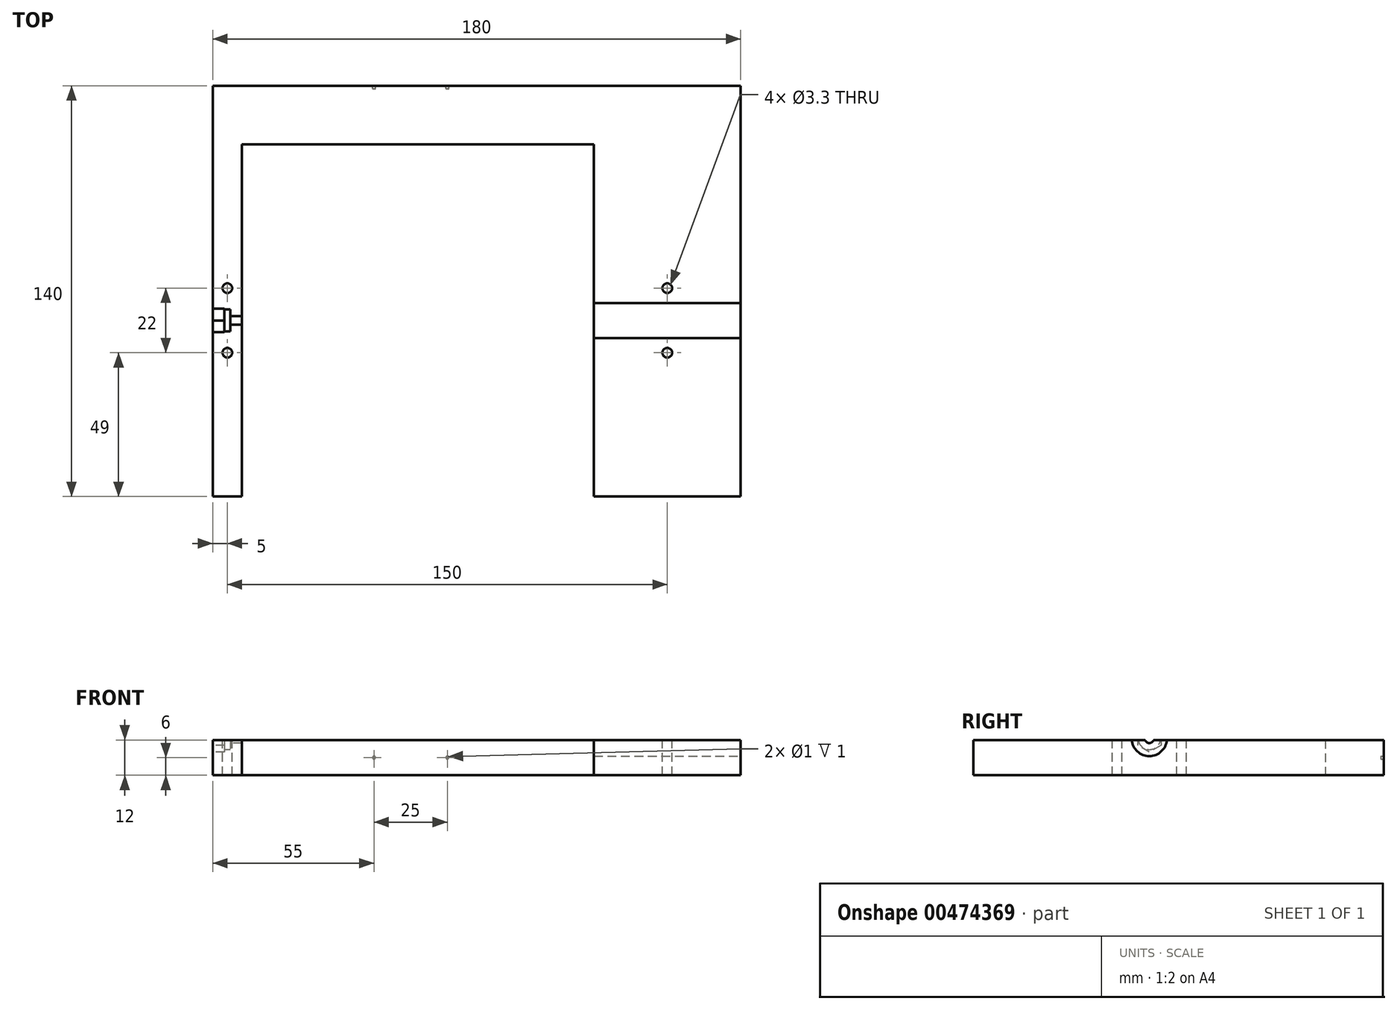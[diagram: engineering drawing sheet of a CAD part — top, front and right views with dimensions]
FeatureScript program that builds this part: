
annotation { "Feature Type Name" : "Feature", "Feature Type Description" : "" }
export const myFeature = defineFeature(function(context is Context, id is Id, definition is map)
    precondition{}
    {
        {
            var Q0;
            Q0=qCreatedBy(makeId("Top.planeOp"),FACE);
            var sketch = newSketch(context, id + "F0", { "sketchPlane" : qUnion([Q0])});
            skLineSegment(sketch, "E0.bottom", {"start": v(-90, -70) * mm, "end": v(90, -70) * mm});
            skLineSegment(sketch, "E0.top", {"start": v(-90, 70) * mm, "end": v(90, 70) * mm});
            skLineSegment(sketch, "E0.left", {"start": v(-90, -70) * mm, "end": v(-90, 70) * mm});
            skLineSegment(sketch, "E0.right", {"start": v(90, -70) * mm, "end": v(90, 70) * mm});
            skPoint(sketch, "E0.middle", {"position": v(0, 0) * mm});
            skSolve(sketch);
        }
        {
            var Q0;
            Q0=qSketchRegion(id+"F0",true);
            extrude(context, id + "F1", {"entities" : qUnion([Q0]), "depth" : 30 * mm});
        }
        {
            var Q0;
            Q0=makeQuery(id+"F1.opExtrude","SWEPT_FACE",FACE,{"disambiguationData":[OSD([sQuery(id+"F0.wireOp",EDGE,"E0.left")])]});
            var sketch = newSketch(context, id + "F2", { "sketchPlane" : qUnion([Q0])});
            skPoint(sketch, "E1.endSnap0", {"position": v(0, 0) * mm});
            skLineSegment(sketch, "E2", {"start": v(-70, 15) * mm, "end": v(-50, 15) * mm, "construction": true});
            skLineSegment(sketch, "E3", {"start": v(70, 0) * mm, "end": v(70, 12.5) * mm, "construction": true});
            skLineSegment(sketch, "E4", {"start": v(70, 12.5) * mm, "end": v(10, 12.5) * mm, "construction": true});
            skLineSegment(sketch, "E5", {"start": v(10, 12.5) * mm, "end": v(10, 17.12) * mm, "construction": true});
            skLineSegment(sketch, "E6", {"start": v(10, 12.5) * mm, "end": v(14, 14.81) * mm, "construction": true});
            skLineSegment(sketch, "E7.MirrorCS", {"start": v(10, 12.5) * mm, "end": v(14, 10.2) * mm, "construction": true});
            skLineSegment(sketch, "E8.MirrorCS", {"start": v(10, 12.5) * mm, "end": v(10, 7.88) * mm, "construction": true});
            skLineSegment(sketch, "E9.MirrorCS", {"start": v(10, 12.5) * mm, "end": v(6, 10.19) * mm, "construction": true});
            skLineSegment(sketch, "E10.MirrorCS", {"start": v(10, 12.5) * mm, "end": v(6, 14.8) * mm, "construction": true});
            skLineSegment(sketch, "E11", {"start": v(6, 14.8) * mm, "end": v(10, 17.12) * mm});
            skLineSegment(sketch, "E12", {"start": v(6, 14.8) * mm, "end": v(6, 10.19) * mm});
            skLineSegment(sketch, "E13", {"start": v(6, 10.19) * mm, "end": v(10, 7.88) * mm});
            skLineSegment(sketch, "E14", {"start": v(10, 7.88) * mm, "end": v(14, 10.2) * mm});
            skLineSegment(sketch, "E15", {"start": v(14, 14.81) * mm, "end": v(14, 10.2) * mm});
            skLineSegment(sketch, "E16", {"start": v(14, 14.81) * mm, "end": v(10, 17.12) * mm});
            skLineSegment(sketch, "E17", {"start": v(6, 14.8) * mm, "end": v(14, 14.81) * mm, "construction": true});
            skSolve(sketch);
        }
        {
            var Q0;
            Q0=qCreatedBy(makeId("Top.planeOp"),FACE);
            var sketch = newSketch(context, id + "F3", { "sketchPlane" : qUnion([Q0])});
            skLineSegment(sketch, "E18", {"start": v(0, 0) * mm, "end": v(0, 50) * mm, "construction": true});
            skLineSegment(sketch, "E19", {"start": v(0, 0) * mm, "end": v(0, -70) * mm, "construction": true});
            skLineSegment(sketch, "E20", {"start": v(0, 0) * mm, "end": v(40, 0) * mm, "construction": true});
            skLineSegment(sketch, "E21", {"start": v(0, 0) * mm, "end": v(-80, 0) * mm, "construction": true});
            skLineSegment(sketch, "E22", {"start": v(40, 0) * mm, "end": v(40, 50) * mm});
            skLineSegment(sketch, "E23", {"start": v(0, 50) * mm, "end": v(40, 50) * mm});
            skLineSegment(sketch, "E24", {"start": v(40, 0) * mm, "end": v(40, -70) * mm});
            skLineSegment(sketch, "E25", {"start": v(0, 50) * mm, "end": v(-80, 50) * mm});
            skLineSegment(sketch, "E26", {"start": v(-80, 50) * mm, "end": v(-80, -70) * mm});
            skLineSegment(sketch, "E27", {"start": v(0, -70) * mm, "end": v(-80, -70) * mm, "construction": true});
            skLineSegment(sketch, "E28", {"start": v(0, -70) * mm, "end": v(74.72, -70) * mm, "construction": true});
            skLineSegment(sketch, "E29", {"start": v(-80, -70) * mm, "end": v(40, -70) * mm});
            skSolve(sketch);
        }
        {
            var Q0;
            Q0 = qSketchRegion(id + "F3", true);
            var Q1;
            Q1=makeQuery(id+"F1.opExtrude","CAP_FACE",FACE,{"disambiguationData":[OSD([sQuery(id+"F0.wireOp",EDGE,"E0.bottom"),sQuery(id+"F0.wireOp",EDGE,"E0.top"),sQuery(id+"F0.wireOp",EDGE,"E0.left"),sQuery(id+"F0.wireOp",EDGE,"E0.right")])],"isStart":false});
            extrude(context, id + "F4", {"entities" : qUnion([Q0]), "operationType" : NewBodyOperationType.REMOVE, "endBound" : BoundingType.UP_TO_SURFACE, "endBoundEntityFace" : qUnion([Q1]), "depth" : 25 * mm});
        }
        {
            var Q0;
            Q0=qSketchRegion(id+"F2",true);
            extrude(context, id + "F5", {"entities" : qUnion([Q0]), "operationType" : NewBodyOperationType.REMOVE, "oppositeDirection" : true, "depth" : 4 * mm});
        }
        {
            var Q0;
            Q0=makeQuery(id+"F5.boolean.opBoolean","COPY",FACE,{"derivedFrom":makeQuery(id+"F5.opExtrude","CAP_FACE",FACE,{"disambiguationData":[OSD([sQuery(id+"F2.wireOp",EDGE,"E11"),sQuery(id+"F2.wireOp",EDGE,"E12"),sQuery(id+"F2.wireOp",EDGE,"E13"),sQuery(id+"F2.wireOp",EDGE,"E14"),sQuery(id+"F2.wireOp",EDGE,"E15"),sQuery(id+"F2.wireOp",EDGE,"E16")])],"isStart":false})});
            var sketch = newSketch(context, id + "F6", { "sketchPlane" : qUnion([Q0])});
            skCircle(sketch, "E30", {"center": v(10, 12.5) * mm, "radius": 3.8 * mm});
            skLineSegment(sketch, "E31", {"start": v(0, 0) * mm, "end": v(10, 0) * mm, "construction": true});
            skLineSegment(sketch, "E32", {"start": v(10, 0) * mm, "end": v(10, 12.5) * mm, "construction": true});
            skSolve(sketch);
        }
        {
            var Q0;
            Q0=qSketchRegion(id+"F6",true);
            var Q1;
            Q1 = qSketchRegion(id + "F8", true);
            extrude(context, id + "F7", {"entities" : qUnion([Q0, Q1]), "operationType" : NewBodyOperationType.REMOVE, "oppositeDirection" : true, "depth" : 2 * mm});
        }
        {
            var Q0;
            Q0=makeQuery(id+"F7.boolean.opBoolean","COPY",FACE,{"derivedFrom":makeQuery(id+"F7.opExtrude","CAP_FACE",FACE,{"disambiguationData":[OSD([sQuery(id+"F6.wireOp",EDGE,"E30")])],"isStart":false})});
            var sketch = newSketch(context, id + "F8", { "sketchPlane" : qUnion([Q0])});
            skLineSegment(sketch, "E33", {"start": v(10, 20.63) * mm, "end": v(10, 4.75) * mm, "construction": true});
            skLineSegment(sketch, "E34", {"start": v(3.02, 8.45) * mm, "end": v(16.9, 16.52) * mm, "construction": true});
            skCircle(sketch, "E35", {"center": v(10, 12.5) * mm, "radius": 1.55 * mm});
            skSolve(sketch);
        }
        {
            var Q0;
            Q0=qSketchRegion(id+"F8",true);
            extrude(context, id + "F9", {"entities" : qUnion([Q0]), "operationType" : NewBodyOperationType.REMOVE, "oppositeDirection" : true, "depth" : 7 * mm});
        }
        {
            var Q0;
            Q0=makeQuery(id+"F1.opExtrude","SWEPT_FACE",FACE,{"disambiguationData":[OSD([sQuery(id+"F0.wireOp",EDGE,"E0.right")])]});
            var sketch = newSketch(context, id + "F10", { "sketchPlane" : qUnion([Q0])});
            skLineSegment(sketch, "E36", {"start": v(-70, 0) * mm, "end": v(-70, 12.5) * mm, "construction": true});
            skLineSegment(sketch, "E37", {"start": v(-70, 12.5) * mm, "end": v(-10, 12.5) * mm, "construction": true});
            skCircle(sketch, "E38", {"center": v(-10, 12.5) * mm, "radius": 6 * mm});
            skSolve(sketch);
        }
        {
            var Q0;
            Q0=makeQuery(id+"F1.opExtrude","SWEPT_FACE",FACE,{"disambiguationData":[OSD([sQuery(id+"F0.wireOp",EDGE,"E0.top")])]});
            var sketch = newSketch(context, id + "F11", { "sketchPlane" : qUnion([Q0])});
            skPoint(sketch, "E39.endSnap0", {"position": v(0, 0) * mm});
            skLineSegment(sketch, "E40", {"start": v(10, 6) * mm, "end": v(35, 6) * mm, "construction": true});
            skCircle(sketch, "E41", {"center": v(35, 6) * mm, "radius": 0.5 * mm});
            skLineSegment(sketch, "E42", {"start": v(0, 0) * mm, "end": v(-5, 0) * mm, "construction": true});
            skLineSegment(sketch, "E43", {"start": v(0, 0) * mm, "end": v(0, 6) * mm, "construction": true});
            skCircle(sketch, "E44", {"center": v(10, 6) * mm, "radius": 0.5 * mm});
            skLineSegment(sketch, "E45", {"start": v(10, 6) * mm, "end": v(-90, 6) * mm, "construction": true});
            skSolve(sketch);
        }
        {
            var Q0;
            Q0=qSketchRegion(id+"F10",true);
            var Q1;
            Q1=makeQuery(id+"F4.boolean.opBoolean","COPY",FACE,{"derivedFrom":makeQuery(id+"F4.opExtrude","SWEPT_FACE",FACE,{"disambiguationData":[OSD([sQuery(id+"F3.wireOp",EDGE,"E22"),sQuery(id+"F3.wireOp",EDGE,"E24")])]})});
            extrude(context, id + "F12", {"entities" : qUnion([Q0]), "operationType" : NewBodyOperationType.REMOVE, "endBound" : BoundingType.UP_TO_SURFACE, "oppositeDirection" : true, "endBoundEntityFace" : qUnion([Q1]), "depth" : 25 * mm});
        }
        {
            var Q0;
            Q0=qSketchRegion(id+"F11",true);
            var Q1;
            Q1=makeQuery(id+"F4.boolean.opBoolean","COPY",FACE,{"derivedFrom":makeQuery(id+"F4.opExtrude","SWEPT_FACE",FACE,{"disambiguationData":[OSD([sQuery(id+"F3.wireOp",EDGE,"YkLpMczh-LnJE-8Oms-Y8Ta-dxZD4QefJqg7")])]})});
            extrude(context, id + "F13", {"entities" : qUnion([Q0]), "operationType" : NewBodyOperationType.REMOVE, "oppositeDirection" : true, "endBoundEntityFace" : qUnion([Q1]), "depth" : 1 * mm});
        }
        {
            var Q0;
            Q0=makeQuery(id+"F1.opExtrude","CAP_FACE",FACE,{"disambiguationData":[OSD([sQuery(id+"F0.wireOp",EDGE,"E0.bottom"),sQuery(id+"F0.wireOp",EDGE,"E0.top"),sQuery(id+"F0.wireOp",EDGE,"E0.left"),sQuery(id+"F0.wireOp",EDGE,"E0.right")])],"isStart":false});
            var sketch = newSketch(context, id + "F14", { "sketchPlane" : qUnion([Q0])});
            skLineSegment(sketch, "E46.bottom", {"start": v(-90, -70) * mm, "end": v(90, -70) * mm});
            skLineSegment(sketch, "E46.top", {"start": v(-90, 70) * mm, "end": v(90, 70) * mm});
            skLineSegment(sketch, "E46.left", {"start": v(-90, -70) * mm, "end": v(-90, 70) * mm});
            skLineSegment(sketch, "E46.right", {"start": v(90, -70) * mm, "end": v(90, 70) * mm});
            skSolve(sketch);
        }
        {
            var Q0;
            Q0=qSketchRegion(id+"F14",true);
            extrude(context, id + "F15", {"entities" : qUnion([Q0]), "operationType" : NewBodyOperationType.REMOVE, "oppositeDirection" : true, "depth" : 18 * mm});
        }
        {
            var Q0;
            {var subQ0=sQuery(id+"F2.wireOp",EDGE,"E12");var subQ1=sQuery(id+"F6.wireOp",EDGE,"E30");Q0=makeQuery(id+"F15.boolean.opBoolean","COPY",FACE,{"disambiguationData":[TD([makeQuery(id+"F1.opExtrude","SWEPT_FACE",FACE,{"disambiguationData":[OSD([sQuery(id+"F0.wireOp",EDGE,"E0.top")])]}),makeQuery(id+"F1.opExtrude","SWEPT_FACE",FACE,{"disambiguationData":[OSD([sQuery(id+"F0.wireOp",EDGE,"E0.left")])]}),makeQuery(id+"F1.opExtrude","SWEPT_FACE",FACE,{"disambiguationData":[OSD([sQuery(id+"F0.wireOp",EDGE,"E0.right")])]}),makeQuery(id+"F4.boolean.opBoolean","COPY",FACE,{"derivedFrom":makeQuery(id+"F4.opExtrude","SWEPT_FACE",FACE,{"disambiguationData":[OSD([sQuery(id+"F3.wireOp",EDGE,"YkLpMczh-LnJE-8Oms-Y8Ta-dxZD4QefJqg7")])]})}),makeQuery(id+"F4.boolean.opBoolean","COPY",FACE,{"derivedFrom":makeQuery(id+"F4.opExtrude","SWEPT_FACE",FACE,{"disambiguationData":[OSD([sQuery(id+"F3.wireOp",EDGE,"0GEvvDHn-DFwf-QAS0-vYnM-1EEuX2mMo1AG")])]})}),makeQuery(id+"F4.boolean.opBoolean","COPY",FACE,{"derivedFrom":makeQuery(id+"F4.opExtrude","SWEPT_FACE",FACE,{"disambiguationData":[OSD([sQuery(id+"F3.wireOp",EDGE,"liEGX8ho-NAPC-Z8Vj-w4bI-YO61ROXNVXDp")])]})}),makeQuery(id+"F5.boolean.opBoolean","COPY",FACE,{"derivedFrom":makeQuery(id+"F5.opExtrude","CAP_FACE",FACE,{"disambiguationData":[OSD([sQuery(id+"F2.wireOp",EDGE,"E11"),subQ0,sQuery(id+"F2.wireOp",EDGE,"E13"),sQuery(id+"F2.wireOp",EDGE,"E14"),sQuery(id+"F2.wireOp",EDGE,"E15"),sQuery(id+"F2.wireOp",EDGE,"E16")])],"isStart":false})}),makeQuery(id+"F5.boolean.opBoolean","COPY",FACE,{"derivedFrom":makeQuery(id+"F5.opExtrude","SWEPT_FACE",FACE,{"disambiguationData":[OSD([subQ0])]})}),makeQuery(id+"F7.boolean.opBoolean","COPY",FACE,{"derivedFrom":makeQuery(id+"F7.opExtrude","SWEPT_FACE",FACE,{"disambiguationData":[OSD([subQ1])]})}),makeQuery(id+"F7.boolean.opBoolean","COPY",FACE,{"derivedFrom":makeQuery(id+"F7.opExtrude","CAP_FACE",FACE,{"disambiguationData":[OSD([subQ1])],"isStart":false})}),makeQuery(id+"F9.boolean.opBoolean","COPY",FACE,{"derivedFrom":makeQuery(id+"F9.opExtrude","SWEPT_FACE",FACE,{"disambiguationData":[OSD([sQuery(id+"F8.wireOp",EDGE,"E35")])]})}),makeQuery(id+"F12.boolean.opBoolean","COPY",FACE,{"derivedFrom":makeQuery(id+"F12.opExtrude","SWEPT_FACE",FACE,{"disambiguationData":[OSD([sQuery(id+"F10.wireOp",EDGE,"E38")])]})})])],"derivedFrom":makeQuery(id+"F15.opExtrude","CAP_FACE",FACE,{"disambiguationData":[OSD([sQuery(id+"F14.wireOp",EDGE,"E46.bottom"),sQuery(id+"F14.wireOp",EDGE,"E46.top"),sQuery(id+"F14.wireOp",EDGE,"E46.left"),sQuery(id+"F14.wireOp",EDGE,"E46.right")])],"isStart":false})});}
            var sketch = newSketch(context, id + "F16", { "sketchPlane" : qUnion([Q0])});
            skPoint(sketch, "E47.middle", {"position": v(0, 0) * mm});
            skLineSegment(sketch, "E48.bottom", {"start": v(90, -70) * mm, "end": v(-90, -70) * mm, "construction": true});
            skLineSegment(sketch, "E48.top", {"start": v(90, 70) * mm, "end": v(-90, 70) * mm, "construction": true});
            skLineSegment(sketch, "E48.left", {"start": v(90, -70) * mm, "end": v(90, 70) * mm, "construction": true});
            skLineSegment(sketch, "E48.right", {"start": v(-90, -70) * mm, "end": v(-90, 70) * mm, "construction": true});
            skLineSegment(sketch, "E49", {"start": v(-90, -70) * mm, "end": v(-85, -70) * mm, "construction": true});
            skLineSegment(sketch, "E50", {"start": v(-85, -70) * mm, "end": v(-85, -10) * mm, "construction": true});
            skLineSegment(sketch, "E51", {"start": v(-85, -10) * mm, "end": v(65, -10) * mm, "construction": true});
            skLineSegment(sketch, "E52", {"start": v(65, -10) * mm, "end": v(65, -70) * mm, "construction": true});
            skLineSegment(sketch, "E53", {"start": v(65, -10) * mm, "end": v(65, 1) * mm, "construction": true});
            skLineSegment(sketch, "E54", {"start": v(65, -10) * mm, "end": v(65, -21) * mm, "construction": true});
            skCircle(sketch, "E55", {"center": v(65, 1) * mm, "radius": 1.65 * mm});
            skCircle(sketch, "E56", {"center": v(65, -21) * mm, "radius": 1.65 * mm});
            skLineSegment(sketch, "E57", {"start": v(-85, -10) * mm, "end": v(-85, 1) * mm, "construction": true});
            skLineSegment(sketch, "E58", {"start": v(-85, -10) * mm, "end": v(-85, -21) * mm, "construction": true});
            skCircle(sketch, "E59", {"center": v(-85, 1) * mm, "radius": 1.65 * mm});
            skCircle(sketch, "E60", {"center": v(-85, -21) * mm, "radius": 1.65 * mm});
            skSolve(sketch);
        }
        {
            var Q0;
            Q0=qSketchRegion(id+"F16",true);
            var Q1;
            Q1=makeQuery(id+"F1.opExtrude","CAP_FACE",FACE,{"disambiguationData":[OSD([sQuery(id+"F0.wireOp",EDGE,"E0.bottom"),sQuery(id+"F0.wireOp",EDGE,"E0.top"),sQuery(id+"F0.wireOp",EDGE,"E0.left"),sQuery(id+"F0.wireOp",EDGE,"E0.right")])],"isStart":true});
            extrude(context, id + "F17", {"entities" : qUnion([Q0]), "operationType" : NewBodyOperationType.REMOVE, "endBound" : BoundingType.UP_TO_SURFACE, "oppositeDirection" : true, "endBoundEntityFace" : qUnion([Q1]), "depth" : 25 * mm});
        }
    });
